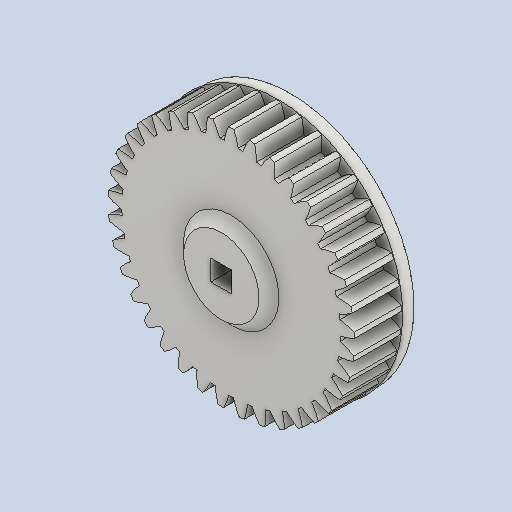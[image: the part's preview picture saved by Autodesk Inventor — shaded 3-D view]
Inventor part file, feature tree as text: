
AUTODESK INVENTOR PART (.ipt)
format: ipt  version: 2022 (Build 260153000, 153)  size: 706,048 bytes
history: native  units: in
note: dims shown in document units (in); Inventor stores cm internally (conversion verified against a paired STEP export)
features: other x12, sketch x5, plane x3
ambient origin geometry x8: Origin, YZ Plane, XZ Plane, XY Plane, X Axis, Y Axis, Z Axis, Center Point
bodies: Solid1 (feature_tree)
feature tree (20):
  other  "Spur Gear2"
  other  "Solid1::Spur Gear2"
  other  "TaggingFeature1"
  sketch  "Sketch1"  dims[d0=0.3937in]
  sketch  "Sketch2"  dims[d9=0.0in]
  sketch  "Sketch3"  dims[d14=0.0in]
  sketch  "Sketch4"  dims[d15=0.9352in]
  sketch  "Sketch5"  dims[d16=0.0in d17=0.0in d18=0.0in d19=0.9352in]
  plane  "XZ Plane_1"
  plane  "Work Plane2"
  plane  "Work Plane3"
  other  "Srf1"
  other  "Srf1::Derived"
  other  "Start plane iMate"
  other  "Distance iMate"
  other  "Position iMate"
  other  "Mesh iMate"
  other  "Axis iMate"
  other  "Mesh iMate2"
  other  "Align iMate"
